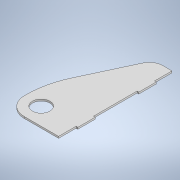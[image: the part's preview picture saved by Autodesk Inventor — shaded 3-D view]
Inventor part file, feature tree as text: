
AUTODESK INVENTOR PART (.ipt)
format: ipt  version: 2022 (Build 260153000, 153)  size: 139,776 bytes
history: native  units: mm
features: fillet x3, other x2, sketch x1
ambient origin geometry x8: Origin, YZ Plane, XZ Plane, XY Plane, X Axis, Y Axis, Z Axis, Center Point
bodies: Solid1 (feature_tree)
feature tree (6):
  other  "Beslag_stempel"
  fillet  "Fillet1"  Radius=45.0mm
  fillet  "Fillet2"  Radius=40.0mm
  fillet  "Fillet3"  Radius=20.0mm
  sketch  "Sketch1"  dims[d3=20.0mm d4=130.0mm d5=20.0mm d6=2.0mm d7=20.5mm d8=103.25mm d9=15.5mm d10=4.363323mm d11=2.0mm d12=2.0mm d13=20.0mm d14=20.0mm d15=20.0mm d16=20.0mm]
  other  "Plate1"
